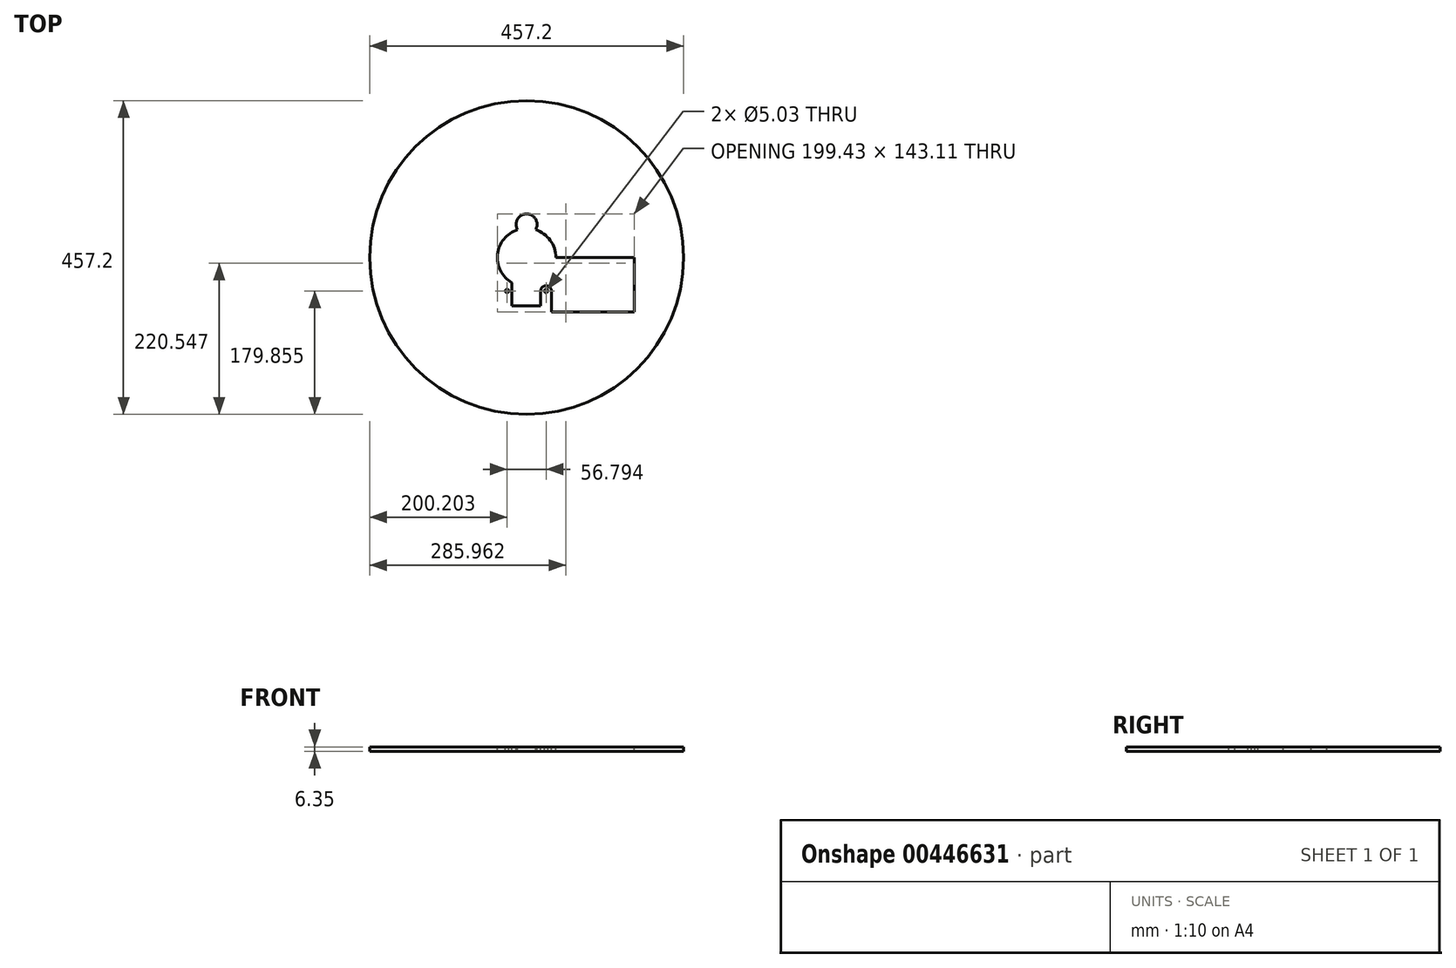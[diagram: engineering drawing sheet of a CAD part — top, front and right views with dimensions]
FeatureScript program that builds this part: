
annotation { "Feature Type Name" : "Feature", "Feature Type Description" : "" }
export const myFeature = defineFeature(function(context is Context, id is Id, definition is map)
    precondition{}
    {
        {
            var Q0;
            Q0=qCreatedBy(makeId("Top.planeOp"),FACE);
            var sketch = newSketch(context, id + "F0", { "sketchPlane" : qUnion([Q0])});
            skCircle(sketch, "E0", {"center": v(0, 0) * mm, "radius": 228.6 * mm});
            skSolve(sketch);
        }
        {
            var Q0;
            Q0 = qSketchRegion(id + "F0", true);
            extrude(context, id + "F1", {"entities" : qUnion([Q0]), "depth" : 6.35 * mm});
        }
        {
            var Q0;
            Q0=makeQuery(id+"F1.opExtrude","CAP_FACE",FACE,{"disambiguationData":[OSD([sQuery(id+"F0.wireOp",EDGE,"E0")])],"isStart":false});
            var sketch = newSketch(context, id + "F2", { "sketchPlane" : qUnion([Q0])});
            skCircle(sketch, "E1", {"center": v(0, 48.72) * mm, "radius": 2.51 * mm});
            skCircle(sketch, "E2", {"center": v(28.4, -48.74) * mm, "radius": 2.51 * mm});
            skCircle(sketch, "E3", {"center": v(-28.4, -48.74) * mm, "radius": 2.51 * mm});
            skLineSegment(sketch, "E4", {"start": v(-28.4, -48.74) * mm, "end": v(28.4, -48.74) * mm, "construction": true});
            skPoint(sketch, "E5", {"position": v(0, -48.74) * mm});
            skSolve(sketch);
        }
        {
            var Q0;
            Q0 = qSketchRegion(id + "F2", true);
            extrude(context, id + "F3", {"entities" : qUnion([Q0]), "operationType" : NewBodyOperationType.REMOVE, "endBound" : BoundingType.UP_TO_NEXT, "oppositeDirection" : true, "depth" : 25.4 * mm});
        }
        {
            var Q0;
            Q0=makeQuery(id+"F1.opExtrude","CAP_FACE",FACE,{"disambiguationData":[OSD([sQuery(id+"F0.wireOp",EDGE,"E0")])],"isStart":false});
            var sketch = newSketch(context, id + "F4", { "sketchPlane" : qUnion([Q0])});
            skArc(sketch, "E6", {"start": v(42.6, 0) * mm, "mid": v(34.46, 25.06) * mm, "end": v(13.13, 40.53) * mm});
            skLineSegment(sketch, "E7.top", {"start": v(-21.61, -70.62) * mm, "end": v(20.65, -70.62) * mm});
            skLineSegment(sketch, "E7.left", {"start": v(-21.61, -36.72) * mm, "end": v(-21.61, -70.62) * mm});
            skLineSegment(sketch, "E7.right", {"start": v(20.65, -48.74) * mm, "end": v(20.65, -70.62) * mm});
            skLineSegment(sketch, "E8.bottom", {"start": v(42.6, 0) * mm, "end": v(157.08, 0) * mm});
            skLineSegment(sketch, "E8.right", {"start": v(157.08, 0) * mm, "end": v(157.08, -79.6) * mm});
            skArc(sketch, "E9", {"start": v(13.13, 40.53) * mm, "mid": v(0, 63.5) * mm, "end": v(-13.13, 40.53) * mm});
            skArc(sketch, "E10.trimOffspring", {"start": v(-13.13, 40.53) * mm, "mid": v(-42.35, 4.65) * mm, "end": v(-21.61, -36.72) * mm});
            skArc(sketch, "E11", {"start": v(36.14, -48.77) * mm, "mid": v(28.41, -41) * mm, "end": v(20.65, -48.74) * mm});
            skLineSegment(sketch, "E12", {"start": v(157.08, -79.6) * mm, "end": v(36.14, -79.6) * mm});
            skLineSegment(sketch, "E13", {"start": v(36.14, -48.72) * mm, "end": v(36.14, -79.6) * mm});
            skSolve(sketch);
        }
        {
            var Q0;
            Q0 = qSketchRegion(id + "F4", true);
            extrude(context, id + "F5", {"entities" : qUnion([Q0]), "operationType" : NewBodyOperationType.REMOVE, "endBound" : BoundingType.UP_TO_NEXT, "oppositeDirection" : true, "depth" : 25.4 * mm});
        }
    });
